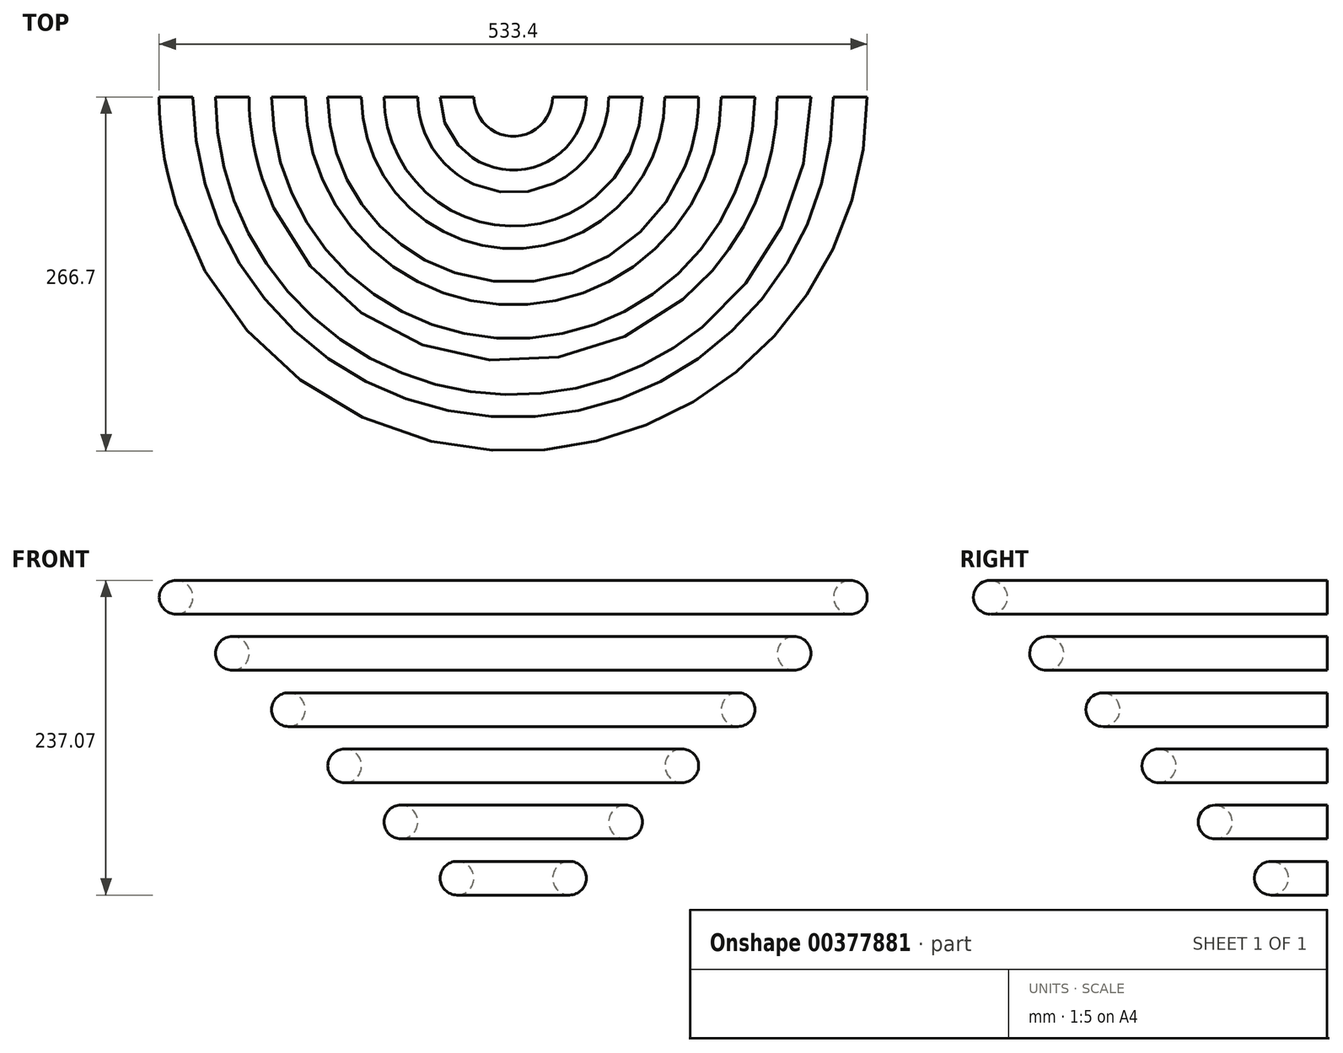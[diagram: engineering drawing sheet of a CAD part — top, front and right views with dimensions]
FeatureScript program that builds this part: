
annotation { "Feature Type Name" : "Feature", "Feature Type Description" : "" }
export const myFeature = defineFeature(function(context is Context, id is Id, definition is map)
    precondition{}
    {
        {
            var Q0;
            Q0=qCreatedBy(makeId("Right.planeOp"),FACE);
            var sketch = newSketch(context, id + "F0", { "sketchPlane" : qUnion([Q0])});
            skLineSegment(sketch, "E0", {"start": v(0, 78.49) * mm, "end": v(0, -85.64) * mm, "construction": true});
            skCircle(sketch, "E1", {"center": v(-127, 0) * mm, "radius": 12.7 * mm});
            skLineSegment(sketch, "E2", {"start": v(0, -127) * mm, "end": v(-282.5, 155.5) * mm, "construction": true});
            skCircle(sketch, "E3", {"center": v(-169.33, 42.33) * mm, "radius": 12.7 * mm});
            skCircle(sketch, "E4", {"center": v(-211.67, 84.67) * mm, "radius": 12.7 * mm});
            skCircle(sketch, "E5", {"center": v(-84.67, -42.33) * mm, "radius": 12.7 * mm});
            skCircle(sketch, "E6", {"center": v(-42.33, -84.67) * mm, "radius": 12.7 * mm});
            skCircle(sketch, "E7", {"center": v(-254, 127) * mm, "radius": 12.7 * mm});
            skLineSegment(sketch, "E8", {"start": v(-42.33, -84.67) * mm, "end": v(0, -127) * mm, "construction": true});
            skLineSegment(sketch, "E9", {"start": v(-84.67, -42.33) * mm, "end": v(-42.33, -84.67) * mm, "construction": true});
            skLineSegment(sketch, "E10", {"start": v(-127, 0) * mm, "end": v(-84.67, -42.33) * mm, "construction": true});
            skLineSegment(sketch, "E11", {"start": v(-127, 0) * mm, "end": v(-169.33, 42.33) * mm, "construction": true});
            skLineSegment(sketch, "E12", {"start": v(-169.33, 42.33) * mm, "end": v(-211.67, 84.67) * mm, "construction": true});
            skLineSegment(sketch, "E13", {"start": v(-254, 127) * mm, "end": v(-211.67, 84.67) * mm, "construction": true});
            skSolve(sketch);
        }
        {
            var Q0;
            Q0=makeQuery(id+"F0.imprint","IMPRINT",FACE,{"disambiguationData":[TD([[makeQuery(id+"F0.imprint","IMPRINT",EDGE,{"derivedFrom":sQuery(id+"F0.wireOp",EDGE,"E6")}),1.0]])]});
            var Q1;
            Q1=sQuery(id+"F0.wireOp",EDGE,"E6");
            var Q2;
            Q2=sQuery(id+"F0.wireOp",EDGE,"E0");
            revolve(context, id + "F1", {"entities" : qUnion([Q0]), "surfaceEntities" : qUnion([Q1]), "axis" : qUnion([Q2]), "revolveType" : RevolveType.SYMMETRIC, "angle" : 180 * degree});
        }
        {
            var Q0;
            Q0=makeQuery(id+"F0.imprint","IMPRINT",FACE,{"disambiguationData":[TD([[makeQuery(id+"F0.imprint","IMPRINT",EDGE,{"derivedFrom":sQuery(id+"F0.wireOp",EDGE,"E5")}),1.0]])]});
            var Q1;
            Q1=sQuery(id+"F0.wireOp",EDGE,"E0");
            revolve(context, id + "F2", {"entities" : qUnion([Q0]), "axis" : qUnion([Q1]), "revolveType" : RevolveType.SYMMETRIC, "angle" : 180 * degree});
        }
        {
            var Q0;
            Q0=makeQuery(id+"F0.imprint","IMPRINT",FACE,{"disambiguationData":[TD([[makeQuery(id+"F0.imprint","IMPRINT",EDGE,{"derivedFrom":sQuery(id+"F0.wireOp",EDGE,"E1")}),1.0]])]});
            var Q1;
            Q1=sQuery(id+"F0.wireOp",EDGE,"E0");
            revolve(context, id + "F3", {"entities" : qUnion([Q0]), "axis" : qUnion([Q1]), "revolveType" : RevolveType.SYMMETRIC, "angle" : 180 * degree});
        }
        {
            var Q0;
            Q0=makeQuery(id+"F0.imprint","IMPRINT",FACE,{"disambiguationData":[TD([[makeQuery(id+"F0.imprint","IMPRINT",EDGE,{"derivedFrom":sQuery(id+"F0.wireOp",EDGE,"E3")}),1.0]])]});
            var Q1;
            Q1=makeQuery(id+"F0.imprint","IMPRINT",FACE,{"disambiguationData":[TD([[makeQuery(id+"F0.imprint","IMPRINT",EDGE,{"derivedFrom":sQuery(id+"F0.wireOp",EDGE,"E4")}),1.0]])]});
            var Q2;
            Q2=makeQuery(id+"F0.imprint","IMPRINT",FACE,{"disambiguationData":[TD([[makeQuery(id+"F0.imprint","IMPRINT",EDGE,{"derivedFrom":sQuery(id+"F0.wireOp",EDGE,"E7")}),1.0]])]});
            var Q3;
            Q3=sQuery(id+"F0.wireOp",EDGE,"E0");
            revolve(context, id + "F4", {"entities" : qUnion([Q0, Q1, Q2]), "axis" : qUnion([Q3]), "revolveType" : RevolveType.SYMMETRIC, "angle" : 180 * degree});
        }
    });
